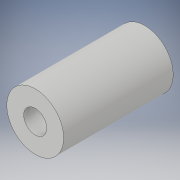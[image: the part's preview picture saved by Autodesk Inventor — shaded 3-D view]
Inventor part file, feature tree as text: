
AUTODESK INVENTOR PART (.ipt)
format: ipt  version: 2018 (Build 220112000, 112)  size: 94,720 bytes
history: native  units: in
note: dims shown in document units (in); Inventor stores cm internally (conversion verified against a paired STEP export)
features: extrude x1, sketch x1
ambient origin geometry x8: Origin, YZ Plane, XZ Plane, XY Plane, X Axis, Y Axis, Z Axis, Center Point
bodies: Solid1 (feature_tree)
feature tree (2):
  extrude  "Extrusion1"  Depth=0.9635in
  sketch  "Sketch1"  dims[d0=0.2031in d1=0.5in d2=0.9635in d3=0.0in]
